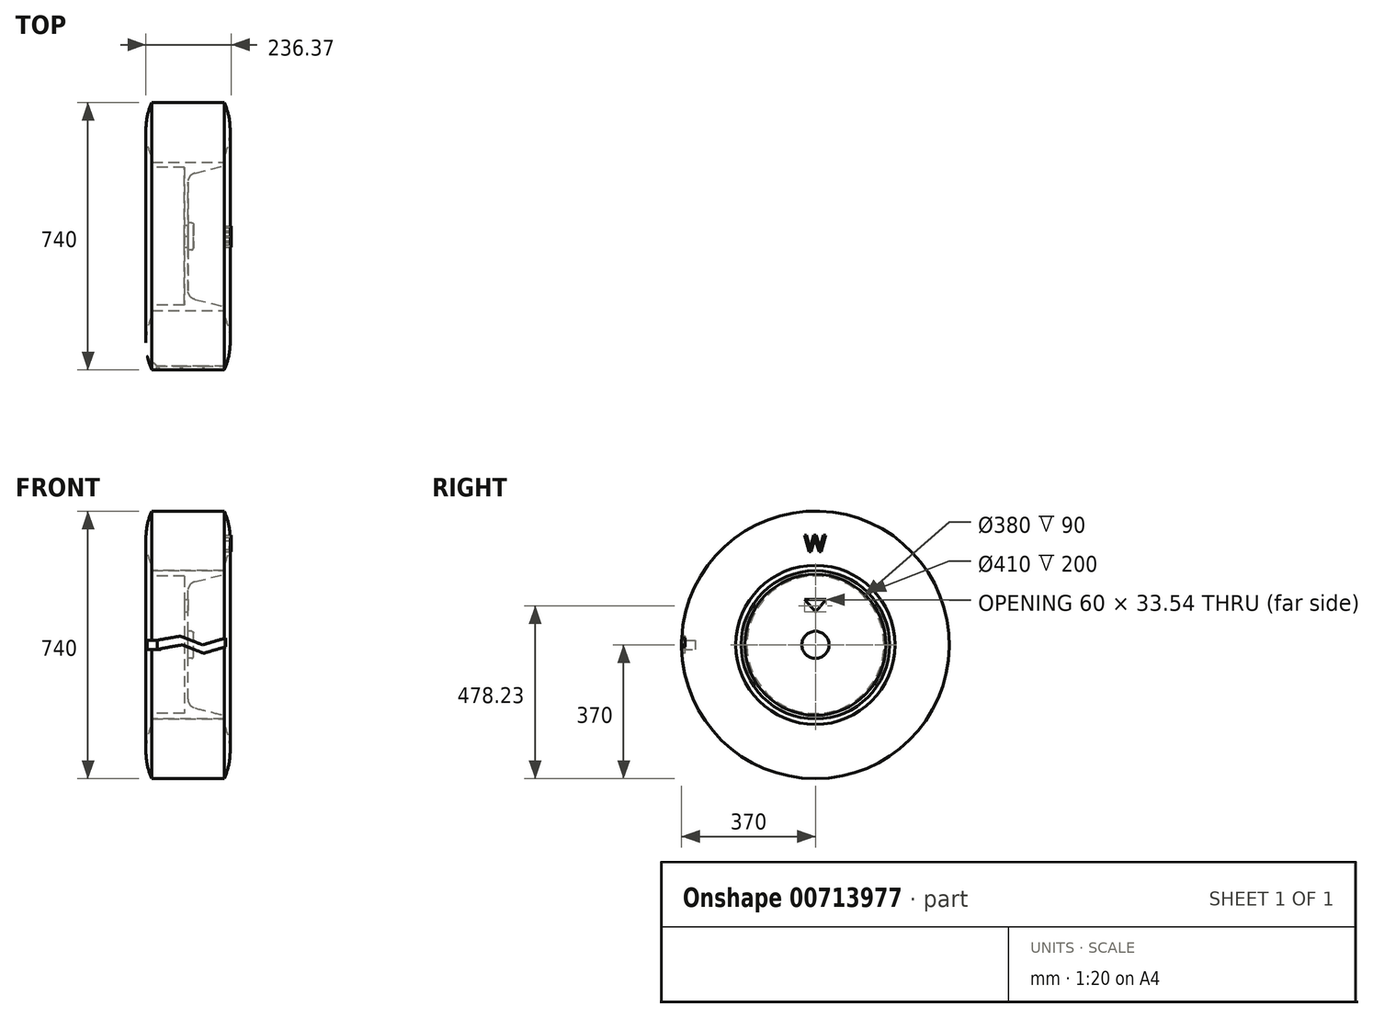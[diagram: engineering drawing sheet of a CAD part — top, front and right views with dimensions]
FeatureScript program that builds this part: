
annotation { "Feature Type Name" : "Feature", "Feature Type Description" : "" }
export const myFeature = defineFeature(function(context is Context, id is Id, definition is map)
    precondition{}
    {
        {
            var Q0;
            Q0=qCreatedBy(makeId("Front.planeOp"),FACE);
            var sketch = newSketch(context, id + "F0", { "sketchPlane" : qUnion([Q0])});
            skLineSegment(sketch, "E0", {"start": v(0, 0) * mm, "end": v(100, 0) * mm});
            skLineSegment(sketch, "E1", {"start": v(100, 0) * mm, "end": v(100, 220) * mm});
            skArc(sketch, "E2", {"start": v(100, 220) * mm, "mid": v(116.37, 295) * mm, "end": v(100, 370) * mm});
            skLineSegment(sketch, "E3", {"start": v(0, 4.06) * mm, "end": v(0, 97.72) * mm, "construction": true});
            skLineSegment(sketch, "E4", {"start": v(100, 370) * mm, "end": v(0, 370) * mm});
            skLineSegment(sketch, "E5.MirrorCS", {"start": v(0, 0) * mm, "end": v(-100, 0) * mm});
            skLineSegment(sketch, "E6.MirrorCS", {"start": v(-100, 0) * mm, "end": v(-100, 220) * mm});
            skArc(sketch, "E7.MirrorCS", {"start": v(-100, 220) * mm, "mid": v(-116.37, 295) * mm, "end": v(-100, 370) * mm});
            skLineSegment(sketch, "E8.MirrorCS", {"start": v(-100, 370) * mm, "end": v(0, 370) * mm});
            skSolve(sketch);
        }
        {
            var Q0;
            Q0=makeQuery(id+"F0.imprint","IMPRINT",FACE,{"disambiguationData":[TD([[makeQuery(id+"F0.imprint","IMPRINT",EDGE,{"derivedFrom":sQuery(id+"F0.wireOp",EDGE,"E0")}),1.0]])]});
            var Q1;
            Q1=sQuery(id+"F0.wireOp",EDGE,"E5.MirrorCS");
            revolve(context, id + "F1", {"entities" : qUnion([Q0]), "axis" : qUnion([Q1]), "revolveType" : RevolveType.FULL});
        }
        {
            var Q0;
            Q0=qCreatedBy(makeId("Top.planeOp"),FACE);
            var sketch = newSketch(context, id + "F2", { "sketchPlane" : qUnion([Q0])});
            skLineSegment(sketch, "E9", {"start": v(-70, -375) * mm, "end": v(-120, -325) * mm});
            skLineSegment(sketch, "E10", {"start": v(-120, -325) * mm, "end": v(-120, -375) * mm});
            skLineSegment(sketch, "E11", {"start": v(-120, -375) * mm, "end": v(-70, -375) * mm});
            skSolve(sketch);
        }
        {
            var Q0;
            Q0=qSketchRegion(id+"F2",true);
            extrude(context, id + "F3", {"entities" : qUnion([Q0]), "operationType" : NewBodyOperationType.REMOVE, "endBound" : BoundingType.SYMMETRIC, "oppositeDirection" : true, "depth" : 25 * mm});
        }
        {
            var Q0;
            Q0=makeQuery(id+"F1.opRevolve","SWEPT_FACE",FACE,{"disambiguationData":[OSD([sQuery(id+"F0.wireOp",EDGE,"E6.MirrorCS")])]});
            var sketch = newSketch(context, id + "F4", { "sketchPlane" : qUnion([Q0])});
            skCircle(sketch, "E12", {"center": v(0, 0) * mm, "radius": 205 * mm});
            skSolve(sketch);
        }
        {
            var Q0;
            Q0=qSketchRegion(id+"F4",true);
            extrude(context, id + "F5", {"entities" : qUnion([Q0]), "operationType" : NewBodyOperationType.REMOVE, "endBound" : BoundingType.THROUGH_ALL, "oppositeDirection" : true, "depth" : 15 * mm});
        }
        {
            var Q0;
            Q0=makeQuery(id+"F3.boolean.opBoolean","INTERSECT",VERTEX,{"derivedFrom":[makeQuery(id+"F1.opRevolve","SWEPT_FACE",FACE,{"disambiguationData":[OSD([sQuery(id+"F0.wireOp",EDGE,"E4"),sQuery(id+"F0.wireOp",EDGE,"E8.MirrorCS")])]}),makeQuery(id+"F1.opRevolve","SWEPT_FACE",FACE,{"disambiguationData":[OSD([sQuery(id+"F0.wireOp",EDGE,"E7.MirrorCS")])]}),makeQuery(id+"F3.opExtrude","CAP_FACE",FACE,{"disambiguationData":[OSD([sQuery(id+"F2.wireOp",EDGE,"E9"),sQuery(id+"F2.wireOp",EDGE,"E10"),sQuery(id+"F2.wireOp",EDGE,"E11")])],"isStart":true})]});
            var Q1;
            {var subQ0=sQuery(id+"F2.wireOp",EDGE,"E9");Q1=makeQuery(id+"F3.boolean.opBoolean","INTERSECT",VERTEX,{"derivedFrom":[makeQuery(id+"F1.opRevolve","SWEPT_FACE",FACE,{"disambiguationData":[OSD([sQuery(id+"F0.wireOp",EDGE,"E4"),sQuery(id+"F0.wireOp",EDGE,"E8.MirrorCS")])]}),makeQuery(id+"F3.opExtrude","SWEPT_FACE",FACE,{"disambiguationData":[OSD([subQ0])]}),makeQuery(id+"F3.opExtrude","CAP_FACE",FACE,{"disambiguationData":[OSD([subQ0,sQuery(id+"F2.wireOp",EDGE,"E10"),sQuery(id+"F2.wireOp",EDGE,"E11")])],"isStart":true})]});}
            var Q2;
            Q2=makeQuery(id+"F3.boolean.opBoolean","INTERSECT",VERTEX,{"derivedFrom":[makeQuery(id+"F1.opRevolve","SWEPT_FACE",FACE,{"disambiguationData":[OSD([sQuery(id+"F0.wireOp",EDGE,"E4"),sQuery(id+"F0.wireOp",EDGE,"E8.MirrorCS")])]}),makeQuery(id+"F1.opRevolve","SWEPT_FACE",FACE,{"disambiguationData":[OSD([sQuery(id+"F0.wireOp",EDGE,"E7.MirrorCS")])]}),makeQuery(id+"F3.opExtrude","CAP_FACE",FACE,{"disambiguationData":[OSD([sQuery(id+"F2.wireOp",EDGE,"E9"),sQuery(id+"F2.wireOp",EDGE,"E10"),sQuery(id+"F2.wireOp",EDGE,"E11")])],"isStart":false})]});
            cPlane(context, id + "F6", {"entities" : qUnion([Q0, Q1, Q2]), "cplaneType" : CPlaneType.THREE_POINT, "offset" : 25 * mm, "width" : 150 * mm, "height" : 150 * mm});
        }
        {
            var Q0;
            Q0=qCreatedBy(id+"F6.planeOp",FACE);
            var sketch = newSketch(context, id + "F7", { "sketchPlane" : qUnion([Q0])});
            skLineSegment(sketch, "E13", {"start": v(-87.6, 12.5) * mm, "end": v(-21.04, 24.08) * mm});
            skLineSegment(sketch, "E14", {"start": v(-21.04, 24.08) * mm, "end": v(40.19, 0) * mm});
            skLineSegment(sketch, "E15", {"start": v(40.19, 0) * mm, "end": v(122.4, 24.08) * mm});
            skLineSegment(sketch, "E16", {"start": v(122.4, 24.08) * mm, "end": v(122.4, 0) * mm});
            skLineSegment(sketch, "E17", {"start": v(122.4, 0) * mm, "end": v(43.22, -23.2) * mm});
            skLineSegment(sketch, "E18", {"start": v(43.22, -23.2) * mm, "end": v(-15.74, 0) * mm});
            skLineSegment(sketch, "E19", {"start": v(-15.74, 0) * mm, "end": v(-87.6, -12.5) * mm});
            skLineSegment(sketch, "E20", {"start": v(-87.6, -12.5) * mm, "end": v(-87.6, 12.5) * mm});
            skSolve(sketch);
        }
        {
            var Q0;
            Q0=qSketchRegion(id+"F7",true);
            extrude(context, id + "F8", {"entities" : qUnion([Q0]), "operationType" : NewBodyOperationType.REMOVE, "oppositeDirection" : true, "depth" : 10 * mm, "hasSecondDirection" : true, "secondDirectionOppositeDirection" : false, "secondDirectionDepth" : 25 * mm});
        }
        {
            var Q0;
            Q0=qSketchRegion(id+"F4",true);
            extrude(context, id + "F9", {"entities" : qUnion([Q0]), "operationType" : NewBodyOperationType.REMOVE, "endBound" : BoundingType.THROUGH_ALL, "oppositeDirection" : true, "depth" : 25 * mm});
        }
        {
            var Q0;
            Q0=qCreatedBy(makeId("Front.planeOp"),FACE);
            var sketch = newSketch(context, id + "F10", { "sketchPlane" : qUnion([Q0])});
            skLineSegment(sketch, "E21", {"start": v(100, 205) * mm, "end": v(100, 195) * mm});
            skLineSegment(sketch, "E22", {"start": v(100, 195) * mm, "end": v(18.94, 174.73) * mm});
            skLineSegment(sketch, "E23", {"start": v(0, 150.48) * mm, "end": v(0, 0) * mm});
            skLineSegment(sketch, "E24", {"start": v(0, 0) * mm, "end": v(-100, 0) * mm});
            skLineSegment(sketch, "E25", {"start": v(100, 205) * mm, "end": v(-100, 205) * mm});
            skLineSegment(sketch, "E26", {"start": v(-100, 0) * mm, "end": v(-100, 205) * mm});
            skPoint(sketch, "E27.visualSharp", {"position": v(0, 170) * mm});
            skArc(sketch, "E27.filletArc", {"start": v(18.94, 174.73) * mm, "mid": v(5.3, 165.87) * mm, "end": v(0, 150.48) * mm});
            skLineSegment(sketch, "E28", {"start": v(0, 0) * mm, "end": v(-177.76, 0) * mm, "construction": true});
            skSolve(sketch);
        }
        {
            var Q0;
            Q0=qSketchRegion(id+"F10",true);
            var Q1;
            Q1=sQuery(id+"F10.wireOp",EDGE,"E28");
            revolve(context, id + "F11", {"entities" : qUnion([Q0]), "axis" : qUnion([Q1]), "revolveType" : RevolveType.FULL});
        }
        {
            var Q0;
            Q0=makeQuery(id+"F11.opRevolve","SWEPT_FACE",FACE,{"disambiguationData":[OSD([sQuery(id+"F10.wireOp",EDGE,"E23")])]});
            var sketch = newSketch(context, id + "F12", { "sketchPlane" : qUnion([Q0])});
            skLineSegment(sketch, "E29", {"start": v(0, 125) * mm, "end": v(-30, 125) * mm});
            skLineSegment(sketch, "E30", {"start": v(-30, 125) * mm, "end": v(0, 91.46) * mm});
            skLineSegment(sketch, "E31", {"start": v(0, 91.46) * mm, "end": v(30, 125) * mm});
            skLineSegment(sketch, "E32", {"start": v(0, 125) * mm, "end": v(30, 125) * mm});
            skSolve(sketch);
        }
        {
            var Q0;
            Q0=qSketchRegion(id+"F12",true);
            extrude(context, id + "F13", {"entities" : qUnion([Q0]), "operationType" : NewBodyOperationType.REMOVE, "endBound" : BoundingType.THROUGH_ALL, "oppositeDirection" : true, "depth" : 25 * mm});
        }
        {
            var Q0;
            Q0=makeQuery(id+"F11.opRevolve","SWEPT_FACE",FACE,{"disambiguationData":[OSD([sQuery(id+"F10.wireOp",EDGE,"E23")])]});
            var sketch = newSketch(context, id + "F14", { "sketchPlane" : qUnion([Q0])});
            skCircle(sketch, "E33", {"center": v(0, 0) * mm, "radius": 37.5 * mm});
            skSolve(sketch);
        }
        {
            var Q0;
            Q0=qSketchRegion(id+"F14",true);
            extrude(context, id + "F15", {"entities" : qUnion([Q0]), "depth" : 15 * mm});
        }
        {
            var Q0;
            Q0=makeQuery(id+"F15.opExtrude","CAP_EDGE",EDGE,{"disambiguationData":[OSD([sQuery(id+"F14.wireOp",EDGE,"E33")])],"isStart":false});
            fillet(context, id + "F16", {"entities" : qUnion([Q0]), "radius" : 5 * mm, "tangentPropagation" : true, "allowEdgeOverflow" : false});
        }
        {
            var Q0;
            Q0=makeQuery(id+"F4.imprint","IMPRINT",FACE,{"disambiguationData":[TD([[makeQuery(id+"F4.imprint","IMPRINT",EDGE,{"derivedFrom":sQuery(id+"F4.wireOp",EDGE,"E12")}),1.0]])]});
            var sketch = newSketch(context, id + "F17", { "sketchPlane" : qUnion([Q0])});
            skCircle(sketch, "E34", {"center": v(0, 0) * mm, "radius": 190 * mm});
            skSolve(sketch);
        }
        {
            var Q0;
            Q0=qSketchRegion(id+"F17",true);
            extrude(context, id + "F18", {"entities" : qUnion([Q0]), "operationType" : NewBodyOperationType.REMOVE, "oppositeDirection" : true, "depth" : 90 * mm});
        }
        {
            var Q0;
            Q0=qCreatedBy(makeId("Right.planeOp"),FACE);
            cPlane(context, id + "F19", {"entities" : qUnion([Q0]), "cplaneType" : CPlaneType.OFFSET, "offset" : 120 * mm, "width" : 150 * mm, "height" : 150 * mm});
        }
        {
            var Q0;
            Q0=qCreatedBy(id+"F19.planeOp",FACE);
            var sketch = newSketch(context, id + "F20", { "sketchPlane" : qUnion([Q0])});
            skCircle(sketch, "E35", {"center": v(0, 0) * mm, "radius": 258.95 * mm, "construction": true});
            skText(sketch, "E36", { "text": "W", "fontName": "OpenSans-Regular.ttf"});
            const initialGuessF20  = {"E36": [-0.031, 0.25709, 1, 0, 0.04668]};
            skSetInitialGuess(sketch, initialGuessF20);
            skSolve(sketch);
        }
        {
            var Q0;
            Q0=qSketchRegion(id+"F20",true);
            extrude(context, id + "F21", {"entities" : qUnion([Q0]), "oppositeDirection" : true, "depth" : 20 * mm});
        }
    });
